# Revit family: SH-4522
name_source: partatom
category: Lighting Fixtures
revit_build: Autodesk Revit 2017 (Build: 20160225_1515(x64)
units: mm (PartAtom-declared; Revit-internal decimal feet)

## family parameters
Cut with Voids When Loaded = No
Host = Face
Light Source = No
Part Type = Normal
Room Calculation Point = No
Round Connector Dimension = Use Diameter
Shared = No

## types (2) — shared parameters
Body Material = Aluminum
Default Elevation = 122 cm
Diffuser = Diffuser
Diffuser Material = Polycarbonate
Height = 245 cm
IP = IPX3
Lamp = E27
Manufacturer = SHOA
Model = SH-4522
Number of Lamps = 2
Protection Class = Class I
URL = https://www.shoaco.com
Voltage/Frequency = 230v/50hz
Wattage. = 0 W
Width = 83 cm
color temperature = 3000K
consumption current = 0 A
website = www.shoaco.com

## type names (no varying parameters)
- SH-4522(Black color-E27)
- SH-4522(White color-E27)

## geometry (parser evidence)
native form markers: Sweep x8
no freeform markers — native parametric forms only
